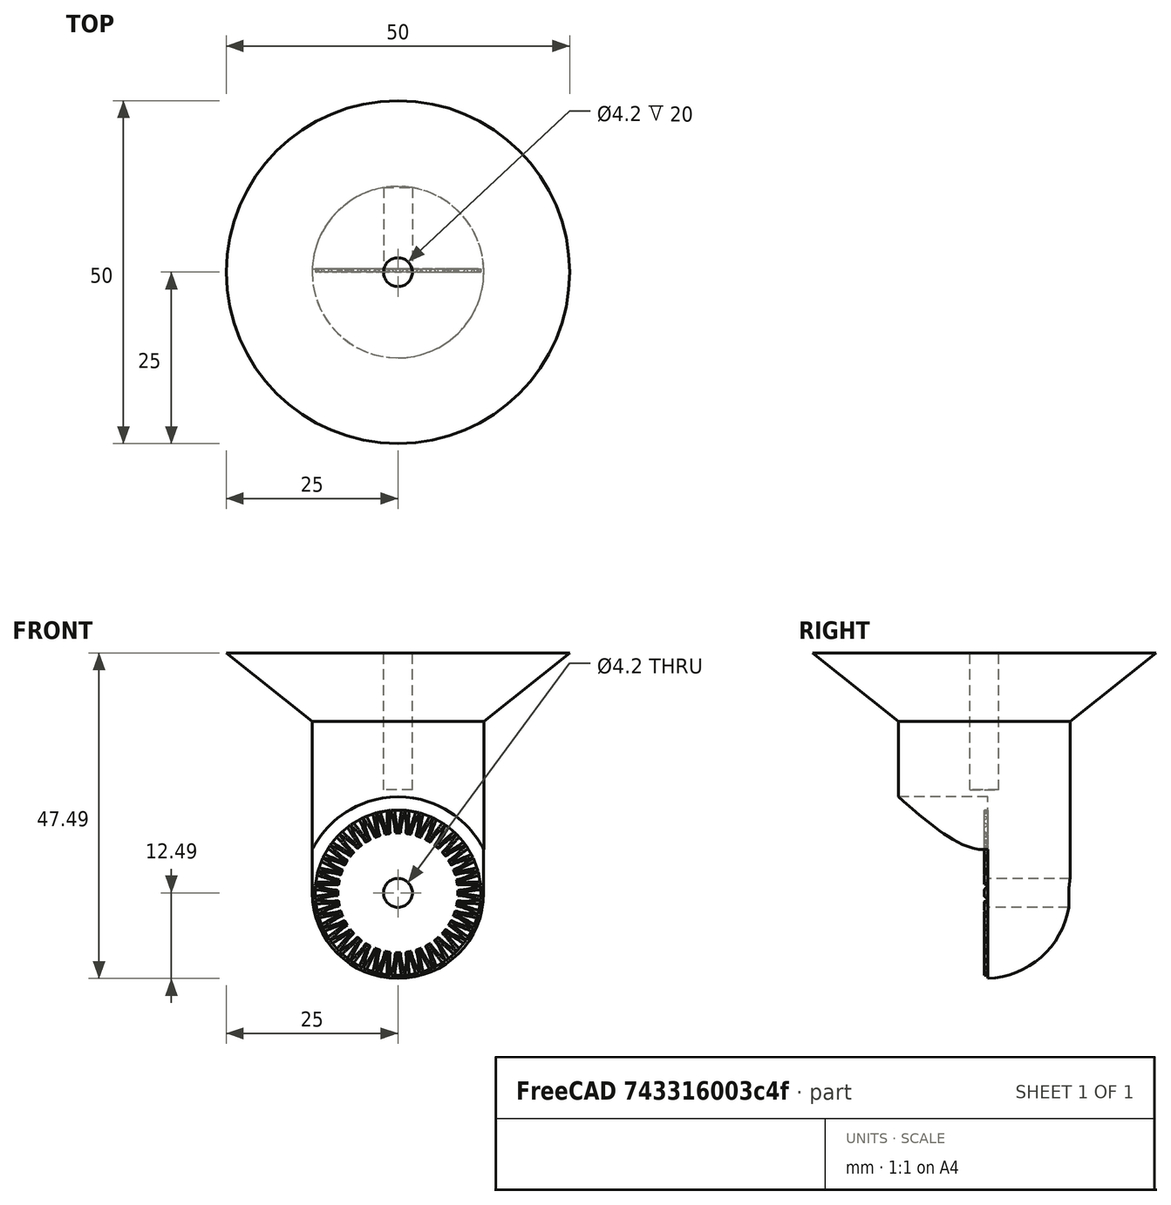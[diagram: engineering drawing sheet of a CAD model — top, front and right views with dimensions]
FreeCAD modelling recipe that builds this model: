
FCSTD DOCUMENT  (FreeCAD 0.18.1R)
Label: DisplayBottom
License: All rights reserved
LicenseURL: http://en.wikipedia.org/wiki/All_rights_reserved
objects: Part::Cylinder×4, Part::Cut×3, Part::MultiFuse×2, Part::Sphere×1, Part::Cone×1, Part::FeaturePython×1
note: 12 computed .brp shape members not serialized (recipe doc carries the construction recipe); baked Part::Feature solids carry a one-line shape summary decoded from their .brp

FEATURE [Part::Sphere] Sphere
  Angle1 = -90
  Angle2 = 90
  Angle3 = 360
  AttacherType = Attacher::AttachEngine3D
  Radius = 12.5
FEATURE [Part::Cylinder] Cylinder
  Angle = 360
  AttacherType = Attacher::AttachEngine3D
  Height = 25
  Radius = 12.5
FEATURE [Part::Cone] Cone
  Angle = 360
  AttacherType = Attacher::AttachEngine3D
  Height = 10
  Placement = pos=(0,0,25) rot=(0,0,1;0rad)
  Radius1 = 12.5
  Radius2 = 25
FEATURE [Part::Cylinder] Cylinder001
  Angle = 360
  AttacherType = Attacher::AttachEngine3D
  Height = 13
  Placement = pos=(0,0.5,0) rot=(1,0,0;1.5708rad)
  Radius = 14
FEATURE [Part::Cylinder] Cylinder002
  Angle = 360
  AttacherType = Attacher::AttachEngine3D
  Height = 13
  Placement = pos=(0,13,0) rot=(1,0,0;1.5708rad)
  Radius = 2.1
FEATURE [Part::Cylinder] Cylinder003
  Angle = 360
  AttacherType = Attacher::AttachEngine3D
  Height = 20
  Placement = pos=(0,0,15) rot=(0,0,1;0rad)
  Radius = 2.1
FEATURE [Part::MultiFuse] Fusion
  Shapes = -> [Sphere,Cylinder,Cone]
FEATURE [Part::Cut] Cut
  Base = -> Fusion
  Tool = -> Cylinder003
FEATURE [Part::Cut] Cut001
  Base = -> Cut
  Tool = -> Cylinder001
FEATURE [Part::Cut] Cut002
  Base = -> Cut001
  Tool = -> Cylinder002
FEATURE [Part::FeaturePython] CrownGear  # WARN: FeaturePython — macro-defined, semantics opaque (R4)
  Placement = pos=(0,1,0) rot=(1,0,0;-1.5708rad)
  construct = true
  height = 2.5
  module = 0.5
  num_profiles = 4
  other_teeth = 36
  pressure_angle = 20
  teeth = 36
  thickness = 0.1
FEATURE [Part::MultiFuse] Fusion001
  Shapes = -> [Cut002,CrownGear]
